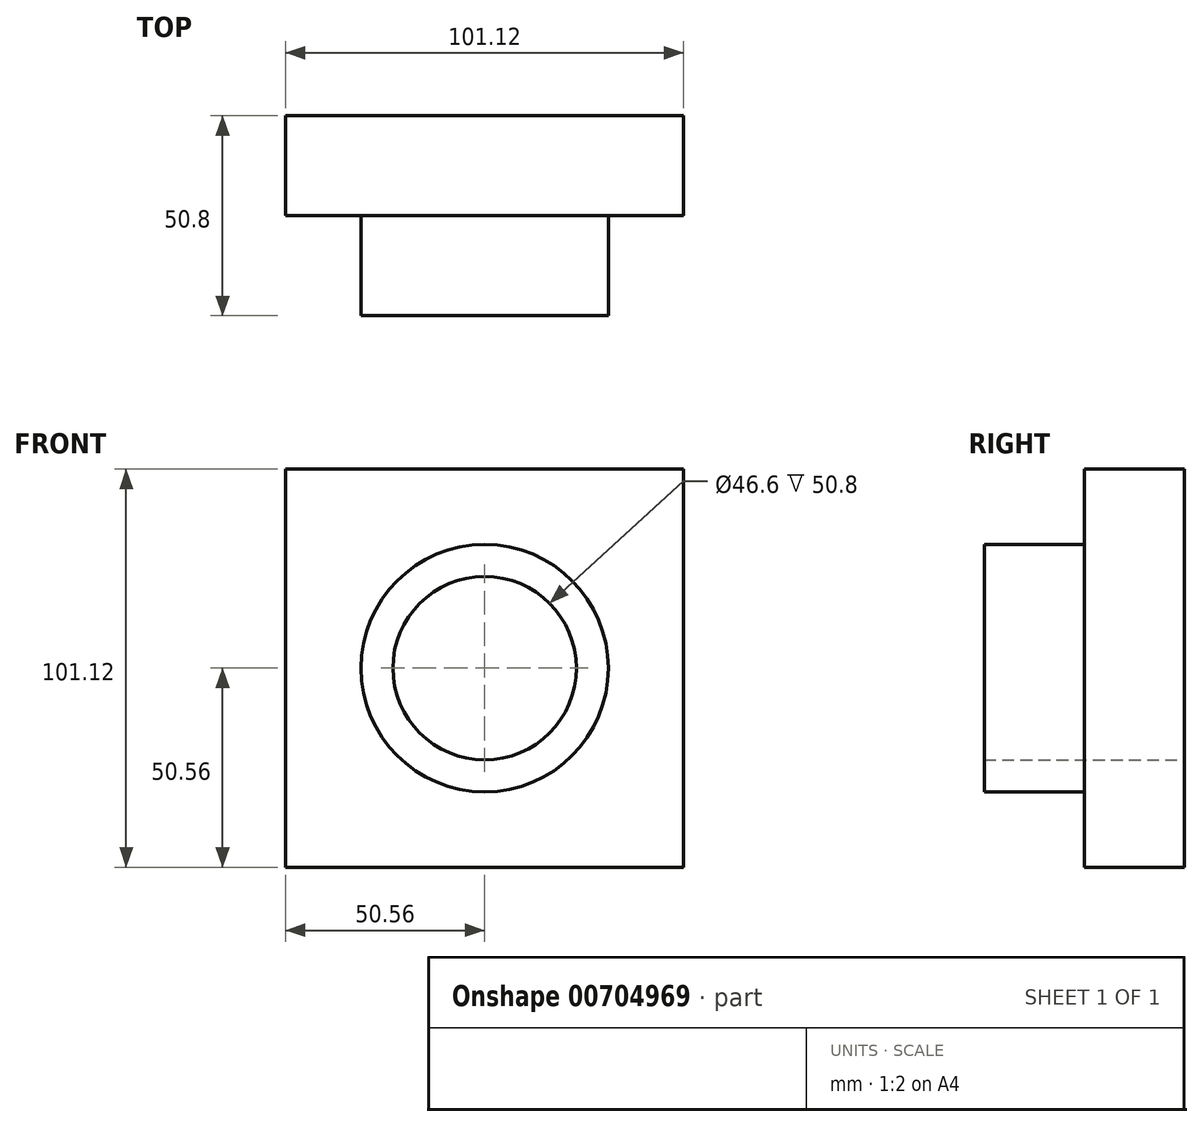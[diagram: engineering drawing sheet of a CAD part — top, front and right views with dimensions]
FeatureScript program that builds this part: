
annotation { "Feature Type Name" : "Feature", "Feature Type Description" : "" }
export const myFeature = defineFeature(function(context is Context, id is Id, definition is map)
    precondition{}
    {
        {
            var Q0;
            Q0=qCreatedBy(makeId("Front.planeOp"),FACE);
            var sketch = newSketch(context, id + "F0", { "sketchPlane" : qUnion([Q0])});
            skLineSegment(sketch, "E0.bottom", {"start": v(-50.56, 50.56) * mm, "end": v(50.56, 50.56) * mm});
            skLineSegment(sketch, "E0.top", {"start": v(-50.56, -50.56) * mm, "end": v(50.56, -50.56) * mm});
            skLineSegment(sketch, "E0.left", {"start": v(-50.56, 50.56) * mm, "end": v(-50.56, -50.56) * mm});
            skLineSegment(sketch, "E0.right", {"start": v(50.56, 50.56) * mm, "end": v(50.56, -50.56) * mm});
            skPoint(sketch, "E0.middle", {"position": v(0, 0) * mm});
            skCircle(sketch, "E1", {"center": v(0, 0) * mm, "radius": 31.42 * mm});
            skCircle(sketch, "E2", {"center": v(0, 0) * mm, "radius": 23.3 * mm});
            skSolve(sketch);
        }
        {
            var Q0;
            Q0=makeQuery(id+"F0.imprint","IMPRINT",FACE,{"disambiguationData":[TD([[makeQuery(id+"F0.imprint","IMPRINT",EDGE,{"derivedFrom":sQuery(id+"F0.wireOp",EDGE,"E0.bottom")}),-1.0]])]});
            extrude(context, id + "F1", {"entities" : qUnion([Q0]), "depth" : 25.4 * mm, "offsetDistance" : 25.4 * mm});
        }
        {
            var Q0;
            Q0=makeQuery(id+"F0.imprint","IMPRINT",FACE,{"disambiguationData":[TD([[makeQuery(id+"F0.imprint","IMPRINT",EDGE,{"derivedFrom":sQuery(id+"F0.wireOp",EDGE,"E1")}),1.0]])]});
            extrude(context, id + "F2", {"entities" : qUnion([Q0]), "operationType" : NewBodyOperationType.ADD, "depth" : 50.8 * mm, "offsetDistance" : 25.4 * mm});
        }
    });
